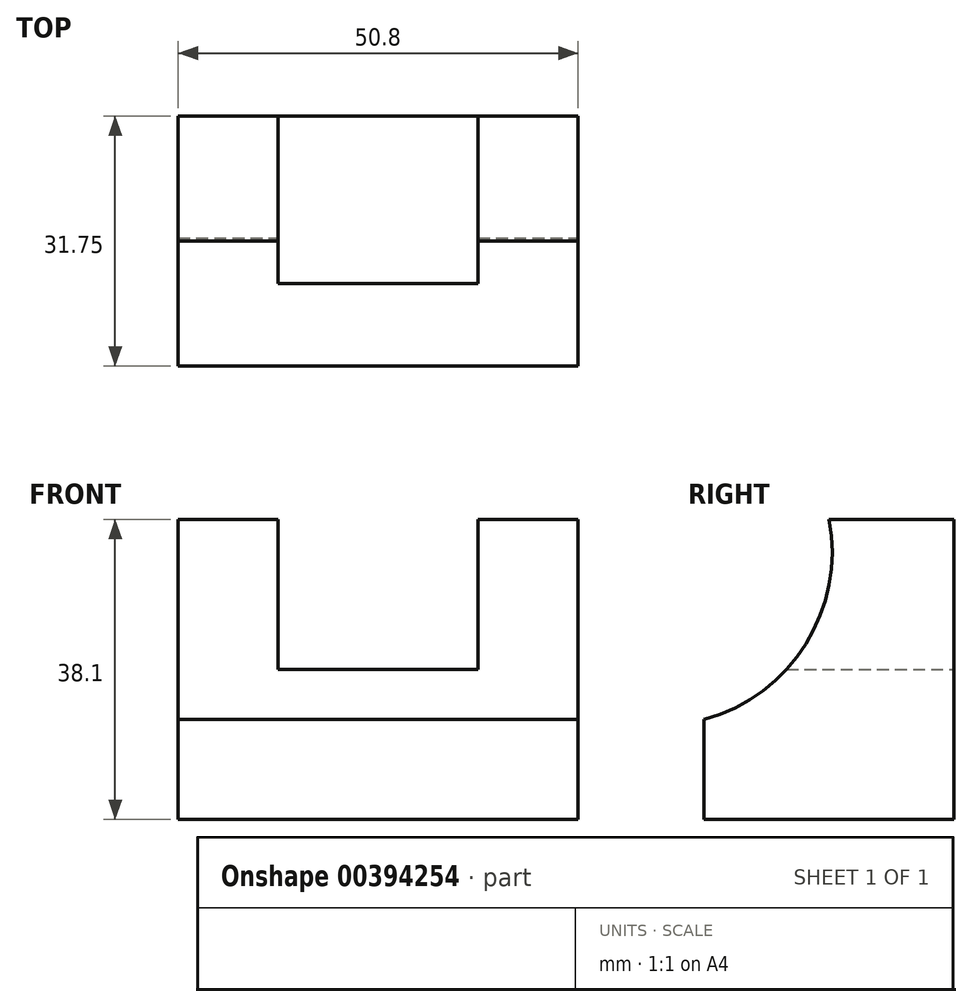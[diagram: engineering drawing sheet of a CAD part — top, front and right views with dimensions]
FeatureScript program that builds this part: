
annotation { "Feature Type Name" : "Feature", "Feature Type Description" : "" }
export const myFeature = defineFeature(function(context is Context, id is Id, definition is map)
    precondition{}
    {
        {
            var Q0;
            Q0=qCreatedBy(makeId("Front.planeOp"),FACE);
            var sketch = newSketch(context, id + "F0", { "sketchPlane" : qUnion([Q0])});
            skLineSegment(sketch, "E0.bottom", {"start": v(0, 0) * mm, "end": v(50.8, 0) * mm});
            skLineSegment(sketch, "E0.top", {"start": v(0, 38.1) * mm, "end": v(50.8, 38.1) * mm});
            skLineSegment(sketch, "E0.left", {"start": v(0, 0) * mm, "end": v(0, 38.1) * mm});
            skLineSegment(sketch, "E0.right", {"start": v(50.8, 0) * mm, "end": v(50.8, 38.1) * mm});
            skSolve(sketch);
        }
        {
            var Q0;
            Q0=makeQuery(id+"F0.imprint","IMPRINT",FACE,{"disambiguationData":[TD([[makeQuery(id+"F0.imprint","IMPRINT",EDGE,{"derivedFrom":sQuery(id+"F0.wireOp",EDGE,"E0.bottom")}),1.0]])]});
            extrude(context, id + "F1", {"entities" : qUnion([Q0]), "depth" : 31.75 * mm});
        }
        {
            var Q0;
            Q0=makeQuery(id+"F1.opExtrude","CAP_FACE",FACE,{"disambiguationData":[OSD([sQuery(id+"F0.wireOp",EDGE,"E0.bottom"),sQuery(id+"F0.wireOp",EDGE,"E0.top"),sQuery(id+"F0.wireOp",EDGE,"E0.left"),sQuery(id+"F0.wireOp",EDGE,"E0.right")])],"isStart":true});
            var sketch = newSketch(context, id + "F2", { "sketchPlane" : qUnion([Q0])});
            skLineSegment(sketch, "E1.bottom", {"start": v(-38.1, 38.1) * mm, "end": v(-12.7, 38.1) * mm});
            skLineSegment(sketch, "E1.top", {"start": v(-38.1, 19.05) * mm, "end": v(-12.7, 19.05) * mm});
            skLineSegment(sketch, "E1.left", {"start": v(-38.1, 38.1) * mm, "end": v(-38.1, 19.05) * mm});
            skLineSegment(sketch, "E1.right", {"start": v(-12.7, 38.1) * mm, "end": v(-12.7, 19.05) * mm});
            skSolve(sketch);
        }
        {
            var Q0;
            Q0=makeQuery(id+"F2.imprint","IMPRINT",FACE,{"disambiguationData":[TD([[makeQuery(id+"F2.imprint","IMPRINT",EDGE,{"derivedFrom":sQuery(id+"F2.wireOp",EDGE,"E1.bottom")}),1.0]])]});
            extrude(context, id + "F3", {"entities" : qUnion([Q0]), "operationType" : NewBodyOperationType.REMOVE, "oppositeDirection" : true, "depth" : 19.05 * mm});
        }
        {
            var Q0;
            Q0=makeQuery(id+"F1.opExtrude","SWEPT_FACE",FACE,{"disambiguationData":[OSD([sQuery(id+"F0.wireOp",EDGE,"E0.right")])]});
            var sketch = newSketch(context, id + "F4", { "sketchPlane" : qUnion([Q0])});
            skArc(sketch, "E2", {"start": v(-31.75, 12.7) * mm, "mid": v(-18.82, 22.28) * mm, "end": v(-15.88, 38.1) * mm});
            skSolve(sketch);
        }
        {
            var Q0;
            {var subQ0=sQuery(id+"F4.wireOp",EDGE,"E2");Q0=makeQuery(id+"F4.imprint","IMPRINT",FACE,{"disambiguationData":[TD([[makeQuery(id+"F4.imprint","IMPRINT",EDGE,{"derivedFrom":subQ0}),1.0]])]});}
            extrude(context, id + "F5", {"entities" : qUnion([Q0]), "operationType" : NewBodyOperationType.REMOVE, "oppositeDirection" : true, "depth" : 50.8 * mm});
        }
        {
            var Q0;
            Q0=makeQuery(id+"F3.boolean.opBoolean","COPY",FACE,{"derivedFrom":makeQuery(id+"F3.opExtrude","CAP_FACE",FACE,{"disambiguationData":[OSD([sQuery(id+"F2.wireOp",EDGE,"E1.bottom"),sQuery(id+"F2.wireOp",EDGE,"E1.top"),sQuery(id+"F2.wireOp",EDGE,"E1.left"),sQuery(id+"F2.wireOp",EDGE,"E1.right")])],"isStart":false})});
            var sketch = newSketch(context, id + "F6", { "sketchPlane" : qUnion([Q0])});
            skLineSegment(sketch, "E3", {"start": v(-38.1, 21.93) * mm, "end": v(-38.1, 19.05) * mm});
            skLineSegment(sketch, "E4", {"start": v(-38.1, 19.05) * mm, "end": v(-12.7, 19.05) * mm});
            skLineSegment(sketch, "E5", {"start": v(-12.7, 19.05) * mm, "end": v(-12.7, 21.93) * mm});
            skLineSegment(sketch, "E6", {"start": v(-12.7, 21.93) * mm, "end": v(-38.1, 21.93) * mm});
            skSolve(sketch);
        }
        {
            var Q0;
            Q0 = qSketchRegion(id + "F6", true);
            extrude(context, id + "F7", {"entities" : qUnion([Q0]), "operationType" : NewBodyOperationType.REMOVE, "oppositeDirection" : true, "depth" : 25.4 * mm});
        }
    });
